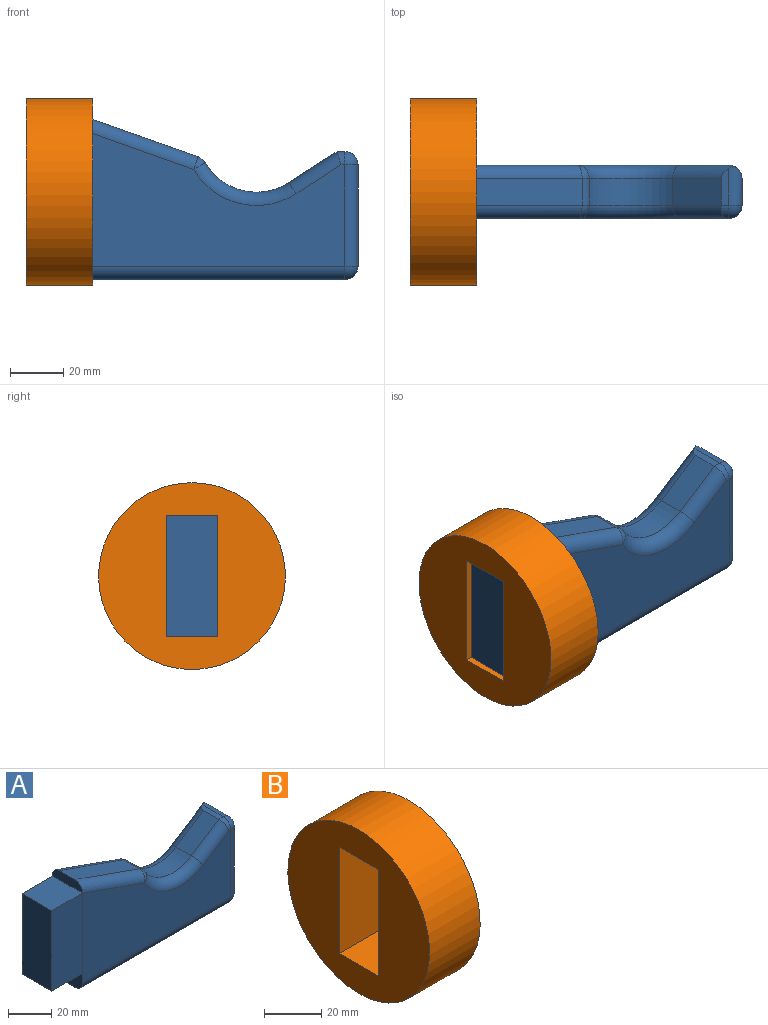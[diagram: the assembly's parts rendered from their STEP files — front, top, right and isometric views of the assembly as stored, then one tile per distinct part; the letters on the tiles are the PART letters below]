
ASSEMBLY  parts=2 mates=1
PART A: 33 faces, bbox 122x20x60.9 mm
  f0: plane 38.03x10mm, normal (1,0,0), area 380.3mm2, adj f10,f14,f15,f24
  f1: plane 60.92x20mm, normal (-1,0,0), area 312mm2, adj f2,f3,f4,f5,f9,f11,f18,f20
  f2: plane 96.98x10mm, normal (0,0,-1), area 969.8mm2, adj f1,f9,f10,f20
  f3: plane 96.98x50.61mm, normal (0,-1,0), area 3345.6mm2, adj f1,f18,f20,f23,f24,f25,f27
  f4: plane 96.98x50.61mm, normal (0,1,0), area 3346.2mm2, adj f1,f9,f11,f13,f14,f16
  f5: plane 42.01x14.89mm, normal (0.33,0,0.94), area 445.7mm2, adj f1,f11,f18,f19
  f6: cylinder r=22.33mm len=31.36mm, axis (0,-1,0), area 360.1mm2, adj f7,f13,f19,f23
  f7: plane 18.09x11.66mm, normal (-0.54,0,0.84), area 215.2mm2, adj f6,f8,f16,f25
  f8: plane 13.62x2.87mm, normal (0,0,1), area 35.9mm2, adj f7,f15,f16,f27
  f9: cylinder r=5mm len=96.98mm, axis (1,0,0), area 761.7mm2, adj f1,f2,f4,f12
  f10: cylinder r=5mm len=10mm, axis (0,-1,0), area 78.5mm2, adj f0,f2,f12,f22
  f11: cylinder r=5mm len=43.68mm, axis (0.94,0,-0.33), area 345mm2, adj f1,f4,f5,f17
  f12: sphere r=5mm, area 39.3mm2, adj f9,f10,f14
  f13: torus R=27.33mm, axis (0,-1,0), area 305.9mm2, adj f4,f6,f16,f17
  f14: cylinder r=5mm len=42.61mm, axis (0,0,1), area 319.3mm2, adj f0,f4,f12,f15,f16
  f15: cylinder r=5mm len=14.58mm, axis (0,1,0), area 102mm2, adj f0,f8,f14,f16,f26
  f16: cylinder r=5mm len=24.06mm, axis (0.84,0,0.54), area 182.2mm2, adj f4,f7,f8,f13,f14,f15
  f17: sphere r=5mm, area 17.5mm2, adj f11,f13,f19
  f18: cylinder r=5mm len=43.68mm, axis (-0.94,0,0.33), area 345mm2, adj f1,f3,f5,f21
  f19: cylinder r=5mm len=10mm, axis (0,-1,0), area 35mm2, adj f5,f6,f17,f21
  f20: cylinder r=5mm len=96.98mm, axis (-1,0,0), area 761.7mm2, adj f1,f2,f3,f22
  f21: sphere r=5mm, area 17.5mm2, adj f18,f19,f23
  f22: sphere r=5mm, area 39.3mm2, adj f10,f20,f24
  f23: torus R=27.33mm, axis (0,-1,0), area 305.9mm2, adj f3,f6,f21,f25
  f24: cylinder r=5mm len=38.03mm, axis (0,0,-1), area 298.7mm2, adj f0,f3,f22,f26
  f25: cylinder r=5mm len=20.8mm, axis (-0.84,0,-0.54), area 164.8mm2, adj f3,f7,f23,f27
  f26: sphere r=5mm, area 39.3mm2, adj f15,f24,f27
  f27: cylinder r=5mm len=5mm, axis (-1,0,0), area 18.4mm2, adj f3,f8,f25,f26
  f28: plane 20x19.41mm, normal (0,0,-1), area 388.2mm2, adj f1,f29,f31,f32
  f29: plane 45.55x20mm, normal (0,-1,0), area 911mm2, adj f1,f28,f30,f32
  f30: plane 20x19.41mm, normal (0,0,1), area 388.2mm2, adj f1,f29,f31,f32
  f31: plane 45.55x20mm, normal (0,1,0), area 911mm2, adj f1,f28,f30,f32
  f32: plane 45.55x19.41mm, normal (-1,0,0), area 884.2mm2, adj f28,f29,f30,f31
PART B: 7 faces, bbox 25x70x70 mm
  f0: plane 45.55x25mm, normal (0,1,0), area 1138.8mm2, adj f1,f3,f5,f6
  f1: plane 25x19.41mm, normal (0,0,1), area 485.3mm2, adj f0,f2,f5,f6
  f2: plane 45.55x25mm, normal (0,-1,0), area 1138.8mm2, adj f1,f3,f5,f6
  f3: plane 25x19.41mm, normal (0,0,-1), area 485.3mm2, adj f0,f2,f5,f6
  f4: cylinder r=35mm len=70mm, axis (1,0,0), area 5497.8mm2, adj f5,f6
  f5: plane 70x70mm, normal (-1,0,0), area 2964.2mm2, adj f0,f1,f2,f3,f4
  f6: plane 70x70mm, normal (1,0,0), area 2964.2mm2, adj f0,f1,f2,f3,f4
PLACE A t=(-31.97,-33.24,-5.02)mm
PLACE B t=(-9.47,-33.24,-5.02)mm
MATE fastened A.f28 <-> B.f1  axis (0,0,-1) through (-92.96,-43.29,-25.42)mm
